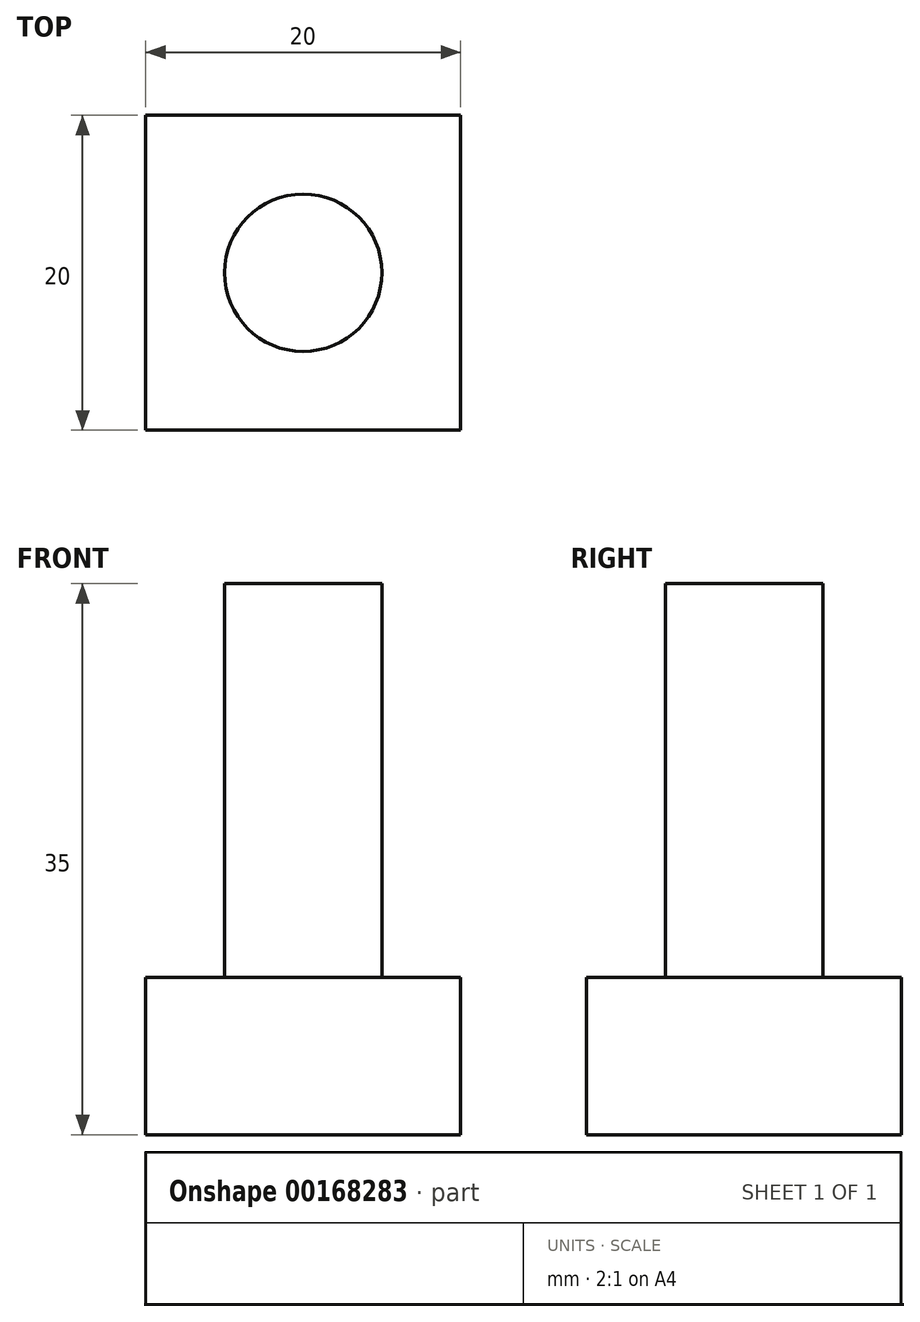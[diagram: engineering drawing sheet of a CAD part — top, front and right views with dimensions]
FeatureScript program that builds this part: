
annotation { "Feature Type Name" : "Feature", "Feature Type Description" : "" }
export const myFeature = defineFeature(function(context is Context, id is Id, definition is map)
    precondition{}
    {
        {
            var Q0;
            Q0=qCreatedBy(makeId("Top.planeOp"),FACE);
            var sketch = newSketch(context, id + "F0", { "sketchPlane" : qUnion([Q0])});
            skLineSegment(sketch, "E0.bottom", {"start": v(10, 10) * mm, "end": v(-10, 10) * mm});
            skLineSegment(sketch, "E0.top", {"start": v(10, -10) * mm, "end": v(-10, -10) * mm});
            skLineSegment(sketch, "E0.left", {"start": v(10, 10) * mm, "end": v(10, -10) * mm});
            skLineSegment(sketch, "E0.right", {"start": v(-10, 10) * mm, "end": v(-10, -10) * mm});
            skPoint(sketch, "E0.middle", {"position": v(0, 0) * mm});
            skSolve(sketch);
        }
        {
            var Q0;
            Q0=qSketchRegion(id+"F0",true);
            extrude(context, id + "F1", {"entities" : qUnion([Q0]), "depth" : 10 * mm});
        }
        {
            var Q0;
            Q0=makeQuery(id+"F1.opExtrude","CAP_FACE",FACE,{"disambiguationData":[OSD([sQuery(id+"F0.wireOp",EDGE,"E0.bottom"),sQuery(id+"F0.wireOp",EDGE,"E0.top"),sQuery(id+"F0.wireOp",EDGE,"E0.left"),sQuery(id+"F0.wireOp",EDGE,"E0.right")])],"isStart":false});
            var sketch = newSketch(context, id + "F2", { "sketchPlane" : qUnion([Q0])});
            skCircle(sketch, "E1", {"center": v(0, 0) * mm, "radius": 5 * mm});
            skSolve(sketch);
        }
        {
            var Q0;
            Q0=makeQuery(id+"F2.imprint","IMPRINT",FACE,{"disambiguationData":[TD([[makeQuery(id+"F2.imprint","IMPRINT",EDGE,{"derivedFrom":sQuery(id+"F2.wireOp",EDGE,"E1")}),1.0]])]});
            var Q1;
            Q1=sQuery(id+"F2.wireOp",EDGE,"E1");
            extrude(context, id + "F3", {"entities" : qUnion([Q0]), "operationType" : NewBodyOperationType.ADD, "surfaceEntities" : qUnion([Q1]), "depth" : 25 * mm});
        }
    });
